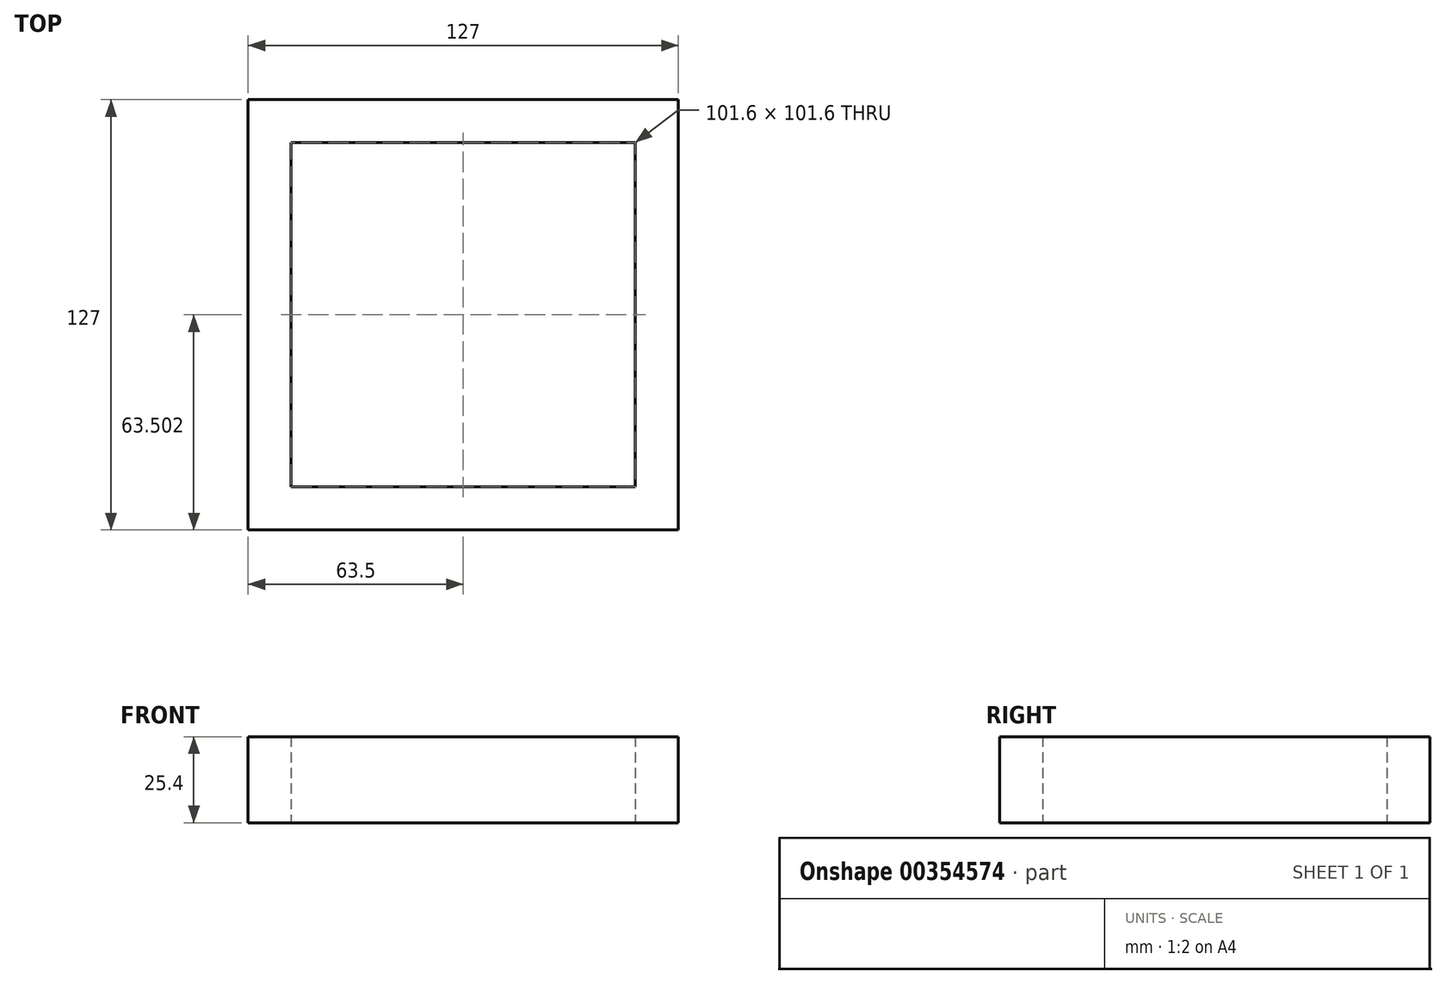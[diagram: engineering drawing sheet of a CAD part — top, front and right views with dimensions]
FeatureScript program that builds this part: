
annotation { "Feature Type Name" : "Feature", "Feature Type Description" : "" }
export const myFeature = defineFeature(function(context is Context, id is Id, definition is map)
    precondition{}
    {
        {
            var Q0;
            Q0=qCreatedBy(makeId("Top.planeOp"),FACE);
            var sketch = newSketch(context, id + "F0", { "sketchPlane" : qUnion([Q0])});
            skLineSegment(sketch, "E0.bottom", {"start": v(-62, 66.24) * mm, "end": v(65, 66.24) * mm});
            skLineSegment(sketch, "E0.top", {"start": v(-62, -60.76) * mm, "end": v(65, -60.76) * mm});
            skLineSegment(sketch, "E0.left", {"start": v(-62, 66.24) * mm, "end": v(-62, -60.76) * mm});
            skLineSegment(sketch, "E0.right", {"start": v(65, 66.24) * mm, "end": v(65, -60.76) * mm});
            skLineSegment(sketch, "E1.0", {"start": v(-49.3, 53.54) * mm, "end": v(52.3, 53.54) * mm});
            skLineSegment(sketch, "E1.1", {"start": v(-49.3, 53.54) * mm, "end": v(-49.3, -48.06) * mm});
            skLineSegment(sketch, "E1.2", {"start": v(-49.3, -48.06) * mm, "end": v(52.3, -48.06) * mm});
            skLineSegment(sketch, "E1.3", {"start": v(52.3, 53.54) * mm, "end": v(52.3, -48.06) * mm});
            skSolve(sketch);
        }
        {
            var Q0;
            Q0=makeQuery(id+"F0.imprint","IMPRINT",FACE,{"disambiguationData":[TD([[makeQuery(id+"F0.imprint","IMPRINT",EDGE,{"derivedFrom":sQuery(id+"F0.wireOp",EDGE,"E0.bottom")}),-1.0]])]});
            extrude(context, id + "F1", {"entities" : qUnion([Q0]), "depth" : 25.4 * mm});
        }
    });
